# Revit family: D9525-DN20-RFA2019
name_source: partatom
category: Pipe Accessories
units: mm (PartAtom-declared; Revit-internal decimal feet)

## family parameters
Always vertical = Yes
Cut with Voids When Loaded = No
Part Type = Valve - Breaks Into
Round Connector Dimension = Use Diameter
Shared = No
Work Plane-Based = No

## types (4) — shared parameters
BBVIS = No
CAT = No
CAT0 = Yes
CenSd_R8_6 = 5 mm  [stored 0.0164042 ft]
ENBL350 = No
L1 = 18 mm  [stored 0.0590551 ft]
L1__ve = -18 mm  [stored -0.0590551 ft]
L2 = 5 mm  [stored 0.0164042 ft]
L2D_Min = 30 mm  [stored 0.0984252 ft]
L2__ve = -5 mm  [stored -0.0164042 ft]
L3 = 23 mm
LC = 10 mm  [stored 0.0328084 ft]
LLDAndHLD = Yes
LLDONLY = Yes
MC Enable LOD 200 = No
MC Enable LOD 350 = No
Manufacturer = Hydronix
QmdConnectorList = 301;D;302;D
R1 = 9 mm  [stored 0.0295276 ft]
R11 = 5 mm  [stored 0.0164042 ft]
R8 = 6 mm  [stored 0.019685 ft]
R9 = 5 mm  [stored 0.0164042 ft]
RT = 2 mm  [stored 0.00656168 ft]
Type Comments = závitový; PN10 (-10~+120°C) nebo PN20 (-10~+80°C)
URL = www.hydronix.cz
V = 40 mm  [stored 0.131234 ft]
V2 = 18 mm  [stored 0.0590551 ft]
V22 = 16 mm  [stored 0.0524934 ft]
VIS0 = No
X0 = 18 mm  [stored 0.0590551 ft]
ZN = 2 mm  [stored 0.00656168 ft]
magiPartTypeId = 304
magiProductFamilyId = ec630ab62332464eb6277f46734e39

## per-type parameters (varying)
- 9525 DN15 NF: CenSd_RN_6=10 mm  [stored 0.0328084 ft]; D=15 mm; DB=27 mm  [stored 0.0885827 ft]; DB1=30 mm  [stored 0.0984252 ft]; DB11=26 mm; Description=Ruční vyvažovací a 2-cestný regulační ventil závitový; bronzový; DN15NF; kvs1,83; HB=51 mm  [stored 0.167323 ft]; HBT=46 mm  [stored 0.150919 ft]; HBT1=23 mm; HBT11=13 mm  [stored 0.0426509 ft]; HBT2=9 mm  [stored 0.0295276 ft]; HBT3=7 mm  [stored 0.0229659 ft]; HBTR=7 mm  [stored 0.0229659 ft]; I=99 mm; I2=50 mm  [stored 0.164042 ft]; I3=45 mm  [stored 0.147638 ft]; I4=27 mm  [stored 0.0885827 ft]; L=83 mm  [stored 0.27231 ft]; L2D=83 mm  [stored 0.27231 ft]; L_2=42 mm; MC Product Code=9525 015 (D9525 DN15NF; kvs=1,83); R=8 mm  [stored 0.0262467 ft]; R2=8 mm  [stored 0.0262467 ft]; R3=9 mm  [stored 0.0295276 ft]; RN=11 mm  [stored 0.0360892 ft]; W2D=15 mm  [stored 0.0492126 ft]; Z1=10 mm  [stored 0.0328084 ft]; Z11=7 mm  [stored 0.0229659 ft]; ZB=11 mm  [stored 0.0360892 ft]; ZB1=9 mm  [stored 0.0295276 ft]; ZZ=10 mm  [stored 0.0328084 ft]; magiProductId=38bc2a49e75f44a19550cf5c31e8d8
- 9525 DN15 LF: CenSd_RN_6=10 mm  [stored 0.0328084 ft]; D=15 mm; DB=27 mm  [stored 0.0885827 ft]; DB1=30 mm  [stored 0.0984252 ft]; DB11=26 mm; Description=Ruční vyvažovací a 2-cestný regulační ventil závitový; bronzový; DN15LF; kvs0,86; HB=51 mm  [stored 0.167323 ft]; HBT=46 mm  [stored 0.150919 ft]; HBT1=23 mm; HBT11=13 mm  [stored 0.0426509 ft]; HBT2=9 mm  [stored 0.0295276 ft]; HBT3=7 mm  [stored 0.0229659 ft]; HBTR=7 mm  [stored 0.0229659 ft]; I=99 mm; I2=50 mm  [stored 0.164042 ft]; I3=45 mm  [stored 0.147638 ft]; I4=27 mm  [stored 0.0885827 ft]; L=83 mm  [stored 0.27231 ft]; L2D=83 mm  [stored 0.27231 ft]; L_2=42 mm; MC Product Code=9525 014 (D9525 DN15LF; kvs=0,86); R=8 mm  [stored 0.0262467 ft]; R2=8 mm  [stored 0.0262467 ft]; R3=9 mm  [stored 0.0295276 ft]; RN=11 mm  [stored 0.0360892 ft]; W2D=15 mm  [stored 0.0492126 ft]; Z1=10 mm  [stored 0.0328084 ft]; Z11=7 mm  [stored 0.0229659 ft]; ZB=11 mm  [stored 0.0360892 ft]; ZB1=9 mm  [stored 0.0295276 ft]; ZZ=10 mm  [stored 0.0328084 ft]; magiProductId=0f0d3c44fff84d33bcc3edb98b3d66
- 9525 DN20: CenSd_RN_6=13 mm  [stored 0.0426509 ft]; D=20 mm; DB=29 mm; DB1=32 mm  [stored 0.104987 ft]; DB11=28 mm; Description=Ruční vyvažovací a 2-cestný regulační ventil závitový; bronzový; DN20; kvs3,47; HB=51 mm  [stored 0.167323 ft]; HBT=52 mm; HBT1=26 mm; HBT11=15 mm  [stored 0.0492126 ft]; HBT2=10 mm  [stored 0.0328084 ft]; HBT3=8 mm  [stored 0.0262467 ft]; HBTR=8 mm  [stored 0.0262467 ft]; I=105 mm; I2=53 mm; I3=48 mm; I4=30 mm  [stored 0.0984252 ft]; L=90 mm  [stored 0.295276 ft]; L2D=90 mm  [stored 0.295276 ft]; L_2=45 mm  [stored 0.147638 ft]; MC Product Code=9525 020 (D9525 DN20; kvs=3,47); R=10 mm  [stored 0.0328084 ft]; R2=11 mm  [stored 0.0360892 ft]; R3=12 mm  [stored 0.0393701 ft]; RN=15 mm  [stored 0.0492126 ft]; W2D=20 mm  [stored 0.0656168 ft]; Z1=10 mm  [stored 0.0328084 ft]; Z11=7 mm  [stored 0.0229659 ft]; ZB=15 mm  [stored 0.0492126 ft]; ZB1=13 mm  [stored 0.0426509 ft]; ZZ=11 mm  [stored 0.0360892 ft]; magiProductId=da587af331304b45b3ec03b8fa0f34
- 9525 DN25: CenSd_RN_6=16 mm  [stored 0.0524934 ft]; D=25 mm; DB=32 mm  [stored 0.104987 ft]; DB1=35 mm; DB11=30 mm  [stored 0.0984252 ft]; Description=Ruční vyvažovací a 2-cestný regulační ventil závitový; bronzový; DN25; kvs6,30; HB=71 mm  [stored 0.23294 ft]; HBT=55 mm; HBT1=28 mm; HBT11=16 mm  [stored 0.0524934 ft]; HBT2=11 mm  [stored 0.0360892 ft]; HBT3=8 mm  [stored 0.0262467 ft]; HBTR=8 mm  [stored 0.0262467 ft]; I=109 mm; I2=55 mm; I3=50 mm  [stored 0.164042 ft]; I4=32 mm  [stored 0.104987 ft]; L=98 mm; L2D=98 mm; L_2=49 mm  [stored 0.160761 ft]; MC Product Code=9525 025 (D9525 DN25; kvs=6,30); R=13 mm  [stored 0.0426509 ft]; R2=13 mm  [stored 0.0426509 ft]; R3=15 mm  [stored 0.0492126 ft]; RN=18 mm  [stored 0.0590551 ft]; W2D=25 mm  [stored 0.082021 ft]; Z1=14 mm  [stored 0.0459318 ft]; Z11=10 mm  [stored 0.0328084 ft]; ZB=18 mm  [stored 0.0590551 ft]; ZB1=16 mm  [stored 0.0524934 ft]; ZZ=12 mm  [stored 0.0393701 ft]; magiProductId=1f5bab54bc3c45cdac322ce9a95cfe

note: [stored X ft] marks values corroborated as IEEE doubles in the binary element streams (Revit-internal decimal feet)

## geometry (parser evidence)
native form markers: Sweep x12
no freeform markers — native parametric forms only
